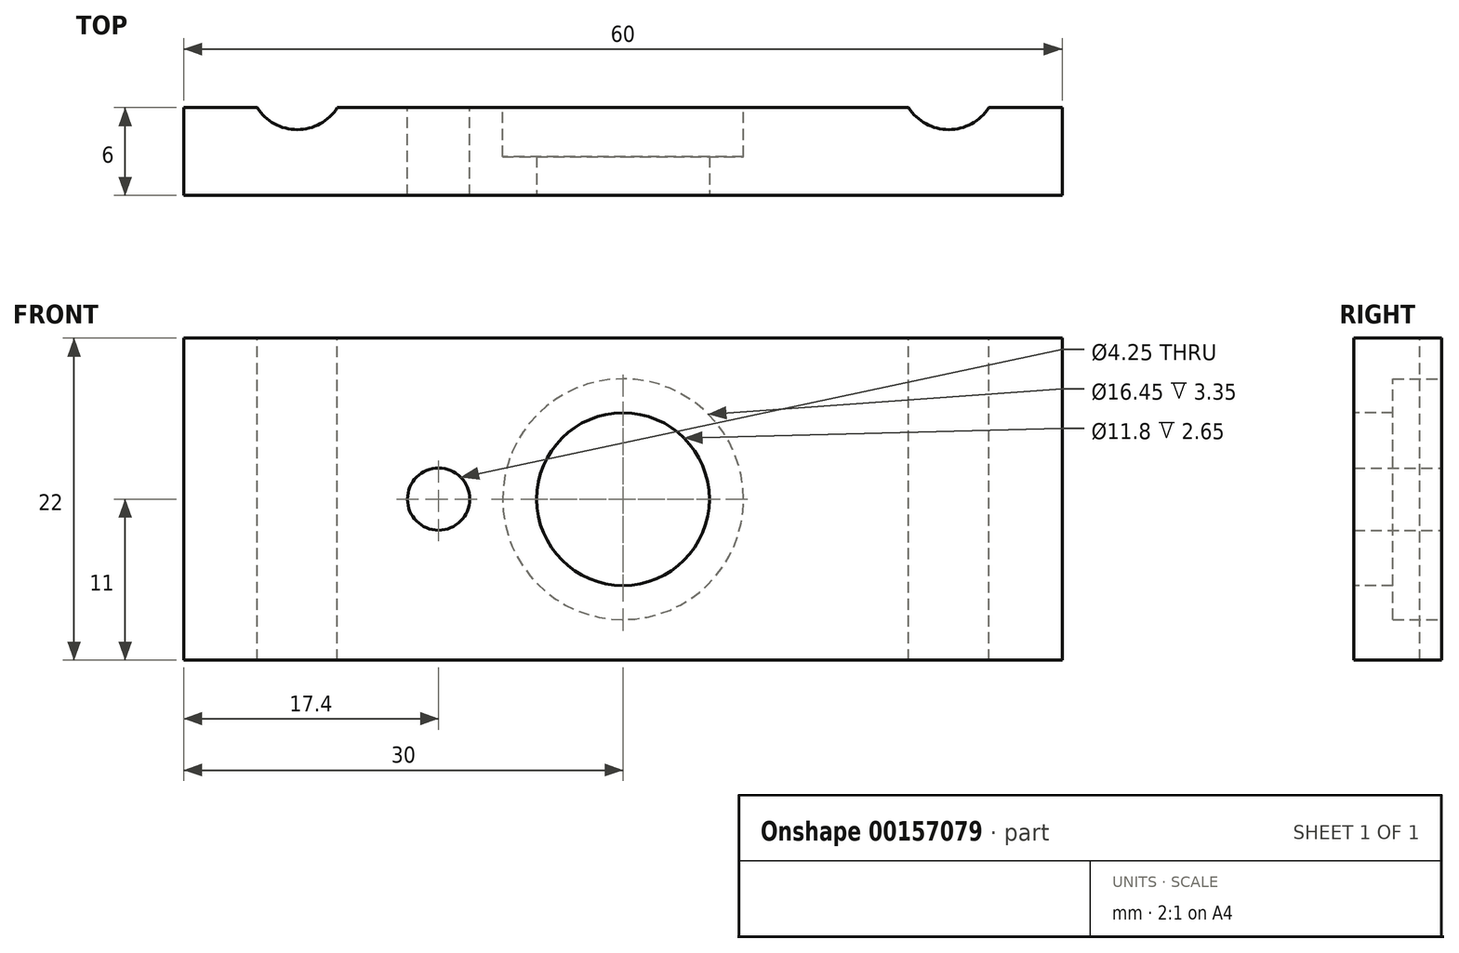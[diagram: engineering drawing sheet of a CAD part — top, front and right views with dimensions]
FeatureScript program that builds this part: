
annotation { "Feature Type Name" : "Feature", "Feature Type Description" : "" }
export const myFeature = defineFeature(function(context is Context, id is Id, definition is map)
    precondition{}
    {
        {
            var Q0;
            Q0=qCreatedBy(makeId("Front.planeOp"),FACE);
            var sketch = newSketch(context, id + "F0", { "sketchPlane" : qUnion([Q0])});
            skLineSegment(sketch, "E0.bottom", {"start": v(30, 11) * mm, "end": v(-30, 11) * mm});
            skLineSegment(sketch, "E0.top", {"start": v(30, -11) * mm, "end": v(-30, -11) * mm});
            skLineSegment(sketch, "E0.left", {"start": v(30, 11) * mm, "end": v(30, -11) * mm});
            skLineSegment(sketch, "E0.right", {"start": v(-30, 11) * mm, "end": v(-30, -11) * mm});
            skPoint(sketch, "E0.middle", {"position": v(0, 0) * mm});
            skCircle(sketch, "E1", {"center": v(0, 0) * mm, "radius": 8.22 * mm});
            skCircle(sketch, "E2", {"center": v(12.6, 0) * mm, "radius": 2.12 * mm});
            skCircle(sketch, "E3.MirrorC", {"center": v(-12.6, 0) * mm, "radius": 2.12 * mm});
            skSolve(sketch);
        }
        {
            var Q0;
            Q0=makeQuery(id+"F0.imprint","IMPRINT",FACE,{"disambiguationData":[TD([[makeQuery(id+"F0.imprint","IMPRINT",EDGE,{"derivedFrom":sQuery(id+"F0.wireOp",EDGE,"E3.MirrorC")}),-1.0]])]});
            var Q1;
            Q1=makeQuery(id+"F0.imprint","IMPRINT",FACE,{"disambiguationData":[TD([[makeQuery(id+"F0.imprint","IMPRINT",EDGE,{"derivedFrom":sQuery(id+"F0.wireOp",EDGE,"E2")}),1.0]])]});
            var Q2;
            Q2=makeQuery(id+"F0.imprint","IMPRINT",FACE,{"disambiguationData":[TD([[makeQuery(id+"F0.imprint","IMPRINT",EDGE,{"derivedFrom":sQuery(id+"F0.wireOp",EDGE,"E1")}),1.0]])]});
            var Q3;
            Q3=makeQuery(id+"F0.imprint","IMPRINT",FACE,{"disambiguationData":[TD([[makeQuery(id+"F0.imprint","IMPRINT",EDGE,{"derivedFrom":sQuery(id+"F0.wireOp",EDGE,"E0.bottom")}),1.0]])]});
            extrude(context, id + "F1", {"entities" : qUnion([Q0, Q1, Q2, Q3]), "depth" : 27 * mm});
        }
        {
            var Q0;
            Q0=makeQuery(id+"F0.imprint","IMPRINT",FACE,{"disambiguationData":[TD([[makeQuery(id+"F0.imprint","IMPRINT",EDGE,{"derivedFrom":sQuery(id+"F0.wireOp",EDGE,"E2")}),1.0]])]});
            var Q1;
            Q1=makeQuery(id+"F0.imprint","IMPRINT",FACE,{"disambiguationData":[TD([[makeQuery(id+"F0.imprint","IMPRINT",EDGE,{"derivedFrom":sQuery(id+"F0.wireOp",EDGE,"E3.MirrorC")}),-1.0]])]});
            var Q2;
            Q2=sQuery(id+"F0.wireOp",EDGE,"E2");
            var Q3;
            Q3=sQuery(id+"F0.wireOp",EDGE,"E3.MirrorC");
            extrude(context, id + "F2", {"entities" : qUnion([Q0, Q1]), "operationType" : NewBodyOperationType.REMOVE, "surfaceEntities" : qUnion([Q2, Q3]), "depth" : 21 * mm});
        }
        {
            var Q0;
            Q0=makeQuery(id+"F1.opExtrude","SWEPT_FACE",FACE,{"disambiguationData":[OSD([sQuery(id+"F0.wireOp",EDGE,"E0.bottom")])]});
            var sketch = newSketch(context, id + "F3", { "sketchPlane" : qUnion([Q0])});
            skCircle(sketch, "E4", {"center": v(22.25, -19.25) * mm, "radius": 3.25 * mm});
            skCircle(sketch, "E5.MirrorC", {"center": v(-22.25, -19.25) * mm, "radius": 3.25 * mm});
            skSolve(sketch);
        }
        {
            var Q0;
            Q0 = qSketchRegion(id + "F3", true);
            extrude(context, id + "F4", {"entities" : qUnion([Q0]), "operationType" : NewBodyOperationType.REMOVE, "endBound" : BoundingType.THROUGH_ALL, "oppositeDirection" : true, "depth" : 25 * mm});
        }
        {
            var Q0;
            Q0=makeQuery(id+"F0.imprint","IMPRINT",FACE,{"disambiguationData":[TD([[makeQuery(id+"F0.imprint","IMPRINT",EDGE,{"derivedFrom":sQuery(id+"F0.wireOp",EDGE,"E1")}),1.0]])]});
            extrude(context, id + "F5", {"entities" : qUnion([Q0]), "operationType" : NewBodyOperationType.REMOVE, "depth" : 24.35 * mm});
        }
        {
            var Q0;
            Q0=makeQuery(id+"F1.opExtrude","CAP_FACE",FACE,{"disambiguationData":[OSD([sQuery(id+"F0.wireOp",EDGE,"E0.bottom"),sQuery(id+"F0.wireOp",EDGE,"E0.top"),sQuery(id+"F0.wireOp",EDGE,"E0.left"),sQuery(id+"F0.wireOp",EDGE,"E0.right")])],"isStart":false});
            var sketch = newSketch(context, id + "F6", { "sketchPlane" : qUnion([Q0])});
            skCircle(sketch, "E6", {"center": v(0, 0) * mm, "radius": 5.9 * mm});
            skSolve(sketch);
        }
        {
            var Q0;
            Q0=makeQuery(id+"F6.imprint","IMPRINT",FACE,{"disambiguationData":[TD([[makeQuery(id+"F6.imprint","IMPRINT",EDGE,{"derivedFrom":sQuery(id+"F6.wireOp",EDGE,"E6")}),1.0]])]});
            extrude(context, id + "F7", {"entities" : qUnion([Q0]), "operationType" : NewBodyOperationType.REMOVE, "endBound" : BoundingType.THROUGH_ALL, "oppositeDirection" : true, "depth" : 25 * mm});
        }
    });
